# Revit family: Mixer_Basin_Nero_Pure
name_source: partatom
category: Plumbing Fixtures
units: mm (PartAtom-declared; Revit-internal decimal feet)

## family parameters
Always vertical = Yes
Cut with Voids When Loaded = Yes
Enable Cutting in Views = No
Maintain Annotation Orientation = No
OmniClass Number = 23.31.00.00
Part Type = Normal
Room Calculation Point = No
Round Connector Dimension = Use Diameter
Shared = No
Work Plane-Based = No

## types (4) — shared parameters
Assembly Code = D2010
CW Connection = Yes
HW Connection = Yes
IfcExportAs = IfcSanitaryTerminal
IfcExportType = NOTDEFINED
Manufacturer = Nero
ManufacturerOverallDepth = 173.5 mm  [stored 0.569226 ft]
ManufacturerOverallHeight = 177.5 mm
ManufacturerOverallWidth = 45 mm  [stored 0.147638 ft]
ModifiedIssue = 20250123 $
URL = https://nerotapware.com.au
Uniclass2015Code = Pr_40_20_87
Uniclass2015Title = Taps and water supply outlet fittings
Uniclass2015Version = Products v1.35
Vent Connection = No
Waste Connection = No
zero-valued in all types: Default Elevation

## per-type parameters (varying)
| type | BodyMaterial | Description | ManufacturerSpecCode | Model | Type Comments |
| Brushed Bronze (NR172201BZ) | Metal_Bronze_Nero_Brushed | Pure SS316L Basin Mixer Brushed Bronze | NR172201BZ | NR172201BZ | Mixer - Basin - Brushed Bronze |
| Graphite (NR172201GR) | Metal_Graphite_Nero_Brushed | Pure SS316L Basin Mixer Graphite | NR172201GR | NR172201GR | Mixer - Basin - Graphite |
| Brushed Gold (NR172201BG) | Metal_Gold_Nero_Brushed | Pure SS316L Basin Mixer Brushed Gold | NR172201BG | NR172201BG | Mixer - Basin - Brushed Gold |
| Brushed Nickel (NR172201BN) | Metal_Nickel_Nero_Brushed | Pure SS316L Basin Mixer Brushed Nickel | NR172201BN | NR172201BN | Mixer - Basin - Brushed Nickel |

note: [stored X ft] marks values corroborated as IEEE doubles in the binary element streams (Revit-internal decimal feet)

## geometry (parser evidence)
native form markers: Sweep x2
no freeform markers — native parametric forms only
